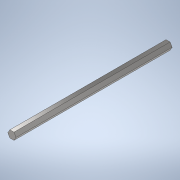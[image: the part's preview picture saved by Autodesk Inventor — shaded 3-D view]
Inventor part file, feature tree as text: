
AUTODESK INVENTOR PART (.ipt)
format: ipt  version: 2020 (Build 240168000, 168)  size: 102,400 bytes
history: native  units: in
note: dims shown in document units (in); Inventor stores cm internally (conversion verified against a paired STEP export)
features: extrude x1, sketch x1
ambient origin geometry x8: Origin, YZ Plane, XZ Plane, XY Plane, X Axis, Y Axis, Z Axis, Center Point
bodies: Solid1 (feature_tree)
feature tree (2):
  extrude  "Extrusion1"  Depth=11.0in TaperAngle=0.0deg
  sketch  "Sketch1"  dims[d0=0.5in d1=11.0in d2=0.0in]
